# Revit family: DC_Holyoake_MEQ_LD-1200-PMF_13
name_source: partatom
category: Air Terminals
revit_build: Autodesk Revit 2013 (Build: 20120221_2030(x64)
units: mm (PartAtom-declared; Revit-internal decimal feet)

## types (1)
- LD-1200-PMF
    Default Elevation = 0 mm  [stored 0 ft]
    Description = Flangeless Linear Bar Diffuser shall be Holyoake Model LD-1200-PMF. Flangeless Linear Bar Diffuser shall be of extruded aluminium construction to the sizes as documented and supplied with Integral Plaster Mounting Frame (PMF) System. Flangeless Linear Bar Diffusers shall be finished in powdercoat and fitted with accessories and dampers where indicated as manufactured by Holyoake.
    Holyoake Product Range = Holyoake Fineline Diffusers
    Manufacturer = Holyoake
    Material Body = Holyoake-Aluminium
    Material Face = Holyoake-Aluminium
    Max Flow = 1200 L/s
    Min Flow = 30 L/s
    Model = LD-1200-PMF
    Noise Level NC Max = 38 NC
    Noise Level NC Min = < 10 NC
    Static Pressure Max = 57.00 Pa
    Static Pressure Min = 3.00 Pa
    Type Comments = Fineline Diffuser Series LD linear bar grilles
    URL = http://www.holyoake.com

note: [stored X ft] marks values corroborated as IEEE doubles in the binary element streams (Revit-internal decimal feet)

## geometry (parser evidence)
native form markers: Blend x6, Sweep x2
no freeform markers — native parametric forms only
